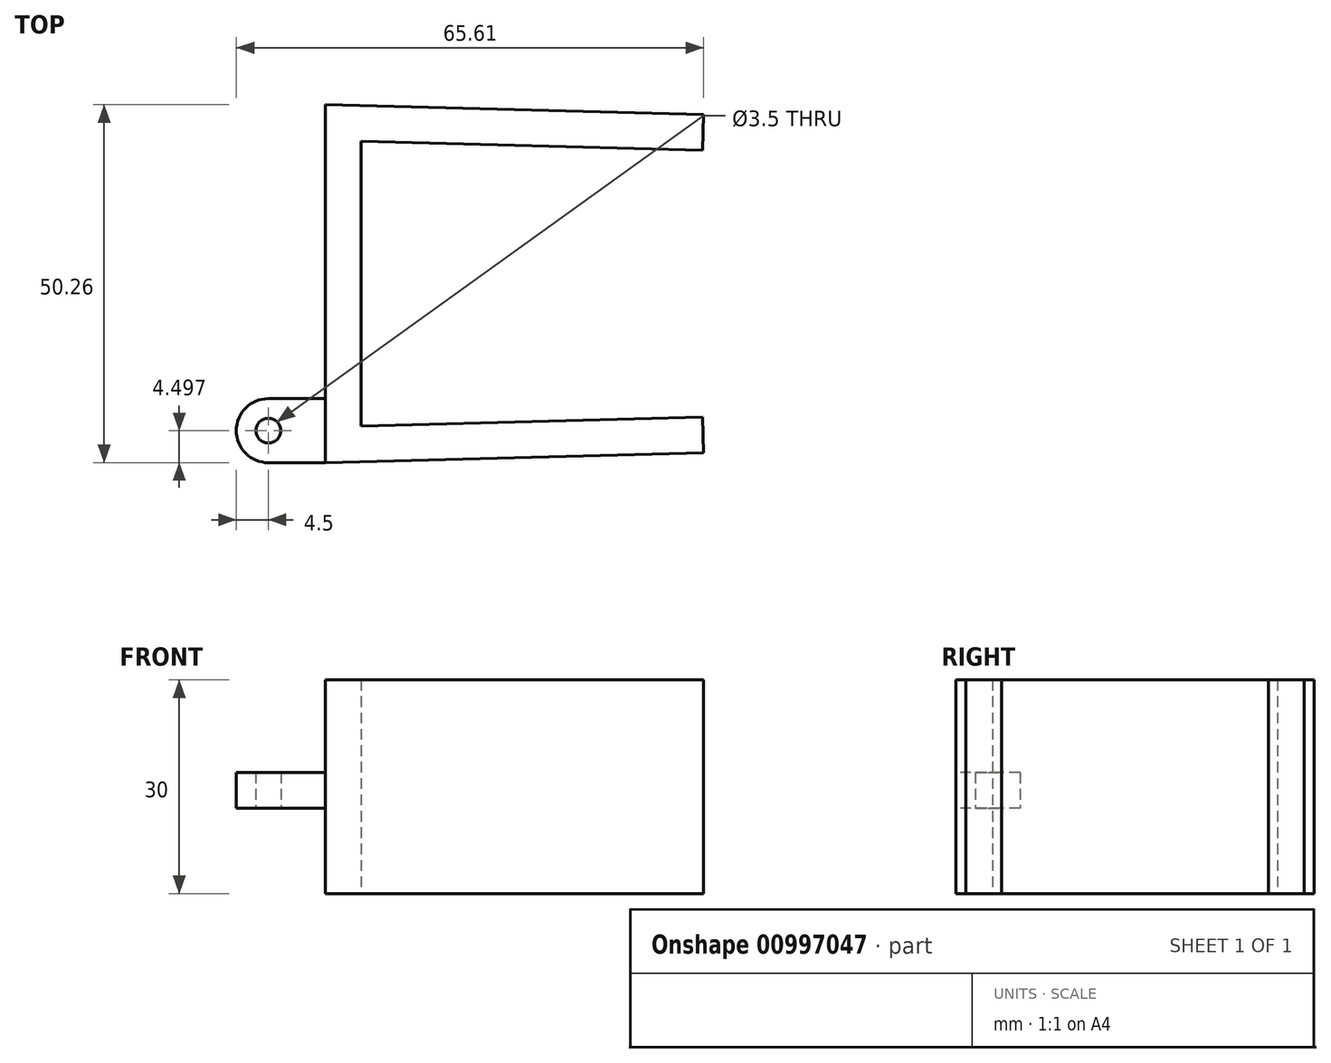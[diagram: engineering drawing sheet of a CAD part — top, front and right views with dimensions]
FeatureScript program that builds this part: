
annotation { "Feature Type Name" : "Feature", "Feature Type Description" : "" }
export const myFeature = defineFeature(function(context is Context, id is Id, definition is map)
    precondition{}
    {
        {
            var Q0;
            Q0=qCreatedBy(makeId("Top.planeOp"),FACE);
            var sketch = newSketch(context, id + "F0", { "sketchPlane" : qUnion([Q0])});
            skLineSegment(sketch, "E0", {"start": v(0, 0) * mm, "end": v(0, 20) * mm});
            skLineSegment(sketch, "E1", {"start": v(0, 20) * mm, "end": v(47.98, 18.74) * mm});
            skLineSegment(sketch, "E2", {"start": v(0, 0) * mm, "end": v(42.4, 0) * mm, "construction": true});
            skLineSegment(sketch, "E3.MirrorCS", {"start": v(0, -20) * mm, "end": v(47.98, -18.74) * mm});
            skLineSegment(sketch, "E4.MirrorCS", {"start": v(0, 0) * mm, "end": v(0, -20) * mm});
            skLineSegment(sketch, "E5.0", {"start": v(-5, 25.13) * mm, "end": v(48.11, 23.74) * mm});
            skLineSegment(sketch, "E5.1", {"start": v(-5, 0) * mm, "end": v(-5, 25.13) * mm});
            skLineSegment(sketch, "E5.2", {"start": v(-5, 0) * mm, "end": v(-5, -25.13) * mm});
            skLineSegment(sketch, "E5.3", {"start": v(-5, -25.13) * mm, "end": v(48.11, -23.74) * mm});
            skLineSegment(sketch, "E6", {"start": v(48.11, 23.74) * mm, "end": v(47.98, 18.74) * mm});
            skLineSegment(sketch, "E7", {"start": v(47.98, -18.74) * mm, "end": v(48.11, -23.74) * mm});
            skSolve(sketch);
        }
        {
            var Q0;
            Q0 = qSketchRegion(id + "F0", true);
            extrude(context, id + "F1", {"entities" : qUnion([Q0]), "depth" : 30 * mm, "offsetDistance" : 25 * mm});
        }
        {
            var Q0;
            Q0=qCreatedBy(makeId("Top.planeOp"),FACE);
            cPlane(context, id + "F2", {"entities" : qUnion([Q0]), "cplaneType" : CPlaneType.OFFSET, "offset" : 12 * mm, "width" : 150 * mm, "height" : 150 * mm});
        }
        {
            var Q0;
            Q0=qCreatedBy(id+"F2.planeOp",FACE);
            var sketch = newSketch(context, id + "F3", { "sketchPlane" : qUnion([Q0])});
            skLineSegment(sketch, "E8", {"start": v(-5, -25.13) * mm, "end": v(-13, -25.13) * mm});
            skArc(sketch, "E9", {"start": v(-13, -16.13) * mm, "mid": v(-17.5, -20.63) * mm, "end": v(-13, -25.13) * mm});
            skCircle(sketch, "E10", {"center": v(-13, -20.63) * mm, "radius": 1.75 * mm});
            skLineSegment(sketch, "E11", {"start": v(-13, -16.13) * mm, "end": v(-5, -16.13) * mm});
            skLineSegment(sketch, "E12", {"start": v(-5, -16.13) * mm, "end": v(-5, -25.13) * mm});
            skSolve(sketch);
        }
        {
            var Q0;
            Q0 = qSketchRegion(id + "F3", true);
            extrude(context, id + "F4", {"entities" : qUnion([Q0]), "operationType" : NewBodyOperationType.ADD, "depth" : 5 * mm, "offsetDistance" : 25 * mm});
        }
    });
